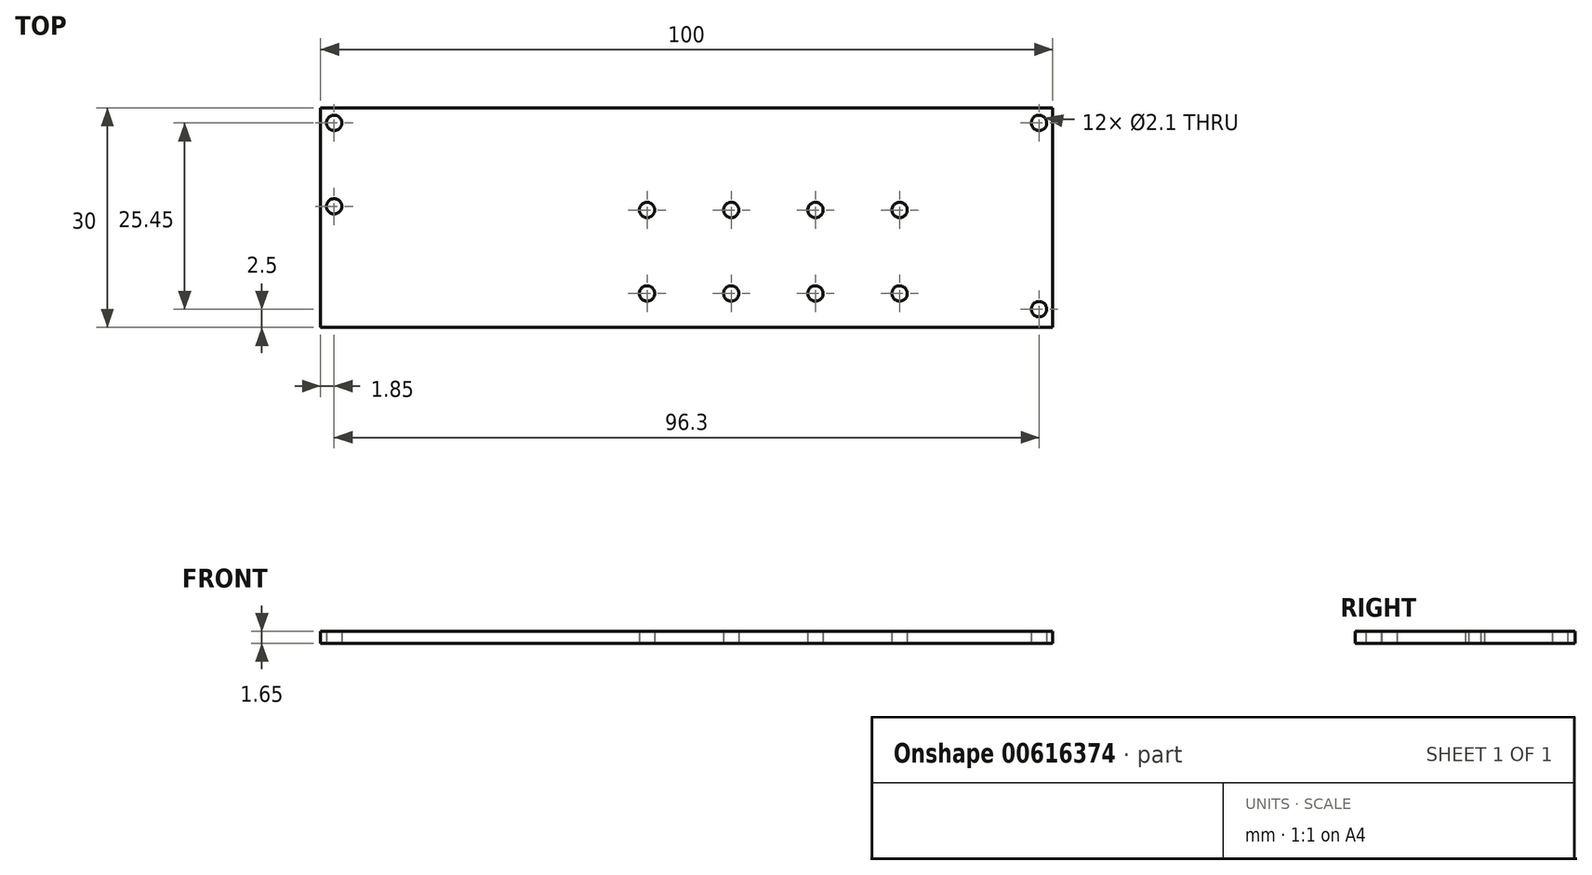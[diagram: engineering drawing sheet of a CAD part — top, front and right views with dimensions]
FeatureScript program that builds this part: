
annotation { "Feature Type Name" : "Feature", "Feature Type Description" : "" }
export const myFeature = defineFeature(function(context is Context, id is Id, definition is map)
    precondition{}
    {
        {
            var Q0;
            Q0=qCreatedBy(makeId("Top.planeOp"),FACE);
            var sketch = newSketch(context, id + "F0", { "sketchPlane" : qUnion([Q0])});
            skLineSegment(sketch, "E0.bottom", {"start": v(50, -15) * mm, "end": v(-50, -15) * mm});
            skLineSegment(sketch, "E0.top", {"start": v(50, 15) * mm, "end": v(-50, 15) * mm});
            skLineSegment(sketch, "E0.left", {"start": v(50, -15) * mm, "end": v(50, 15) * mm});
            skLineSegment(sketch, "E0.right", {"start": v(-50, -15) * mm, "end": v(-50, 15) * mm});
            skPoint(sketch, "E0.middle", {"position": v(0, 0) * mm});
            skCircle(sketch, "E1", {"center": v(-48.15, 12.95) * mm, "radius": 1.05 * mm});
            skCircle(sketch, "E2", {"center": v(-48.15, 1.55) * mm, "radius": 1.05 * mm});
            skCircle(sketch, "E3", {"center": v(6.1, 1.05) * mm, "radius": 1.05 * mm});
            skCircle(sketch, "E4", {"center": v(17.6, 1.05) * mm, "radius": 1.05 * mm});
            skCircle(sketch, "E5", {"center": v(29.1, 1.05) * mm, "radius": 1.05 * mm});
            skCircle(sketch, "E6", {"center": v(29.1, -10.35) * mm, "radius": 1.05 * mm});
            skCircle(sketch, "E7", {"center": v(-5.4, 1.05) * mm, "radius": 1.05 * mm});
            skCircle(sketch, "E8", {"center": v(-5.4, -10.35) * mm, "radius": 1.05 * mm});
            skCircle(sketch, "E9", {"center": v(6.1, -10.35) * mm, "radius": 1.05 * mm});
            skCircle(sketch, "E10", {"center": v(17.6, -10.35) * mm, "radius": 1.05 * mm});
            skCircle(sketch, "E11", {"center": v(48.15, 12.95) * mm, "radius": 1.05 * mm});
            skCircle(sketch, "E12", {"center": v(48.15, -12.5) * mm, "radius": 1.05 * mm});
            skLineSegment(sketch, "E13", {"start": v(48.15, 24.03) * mm, "end": v(48.15, -29.32) * mm, "construction": true});
            skLineSegment(sketch, "E14", {"start": v(63.05, -10.35) * mm, "end": v(-64.33, -10.35) * mm, "construction": true});
            skLineSegment(sketch, "E15", {"start": v(62.73, 1.05) * mm, "end": v(-62.73, 1.05) * mm, "construction": true});
            skLineSegment(sketch, "E16", {"start": v(58.4, 12.95) * mm, "end": v(-64.33, 12.95) * mm, "construction": true});
            skLineSegment(sketch, "E17", {"start": v(-48.15, 26.44) * mm, "end": v(-48.15, -33) * mm, "construction": true});
            skLineSegment(sketch, "E18", {"start": v(-5.4, 26.12) * mm, "end": v(-5.4, -34.93) * mm, "construction": true});
            skLineSegment(sketch, "E19", {"start": v(6.1, 26.44) * mm, "end": v(6.1, -34.93) * mm, "construction": true});
            skLineSegment(sketch, "E20", {"start": v(17.6, 26.76) * mm, "end": v(17.6, -34.93) * mm, "construction": true});
            skLineSegment(sketch, "E21", {"start": v(29.1, 26.6) * mm, "end": v(29.1, -34.93) * mm, "construction": true});
            skSolve(sketch);
        }
        {
            var Q0;
            Q0=makeQuery(id+"F0.imprint","IMPRINT",FACE,{"disambiguationData":[TD([[makeQuery(id+"F0.imprint","IMPRINT",EDGE,{"derivedFrom":sQuery(id+"F0.wireOp",EDGE,"E0.bottom")}),-1.0]])]});
            extrude(context, id + "F1", {"entities" : qUnion([Q0]), "depth" : 1.65 * mm, "offsetDistance" : 25 * mm});
        }
    });
